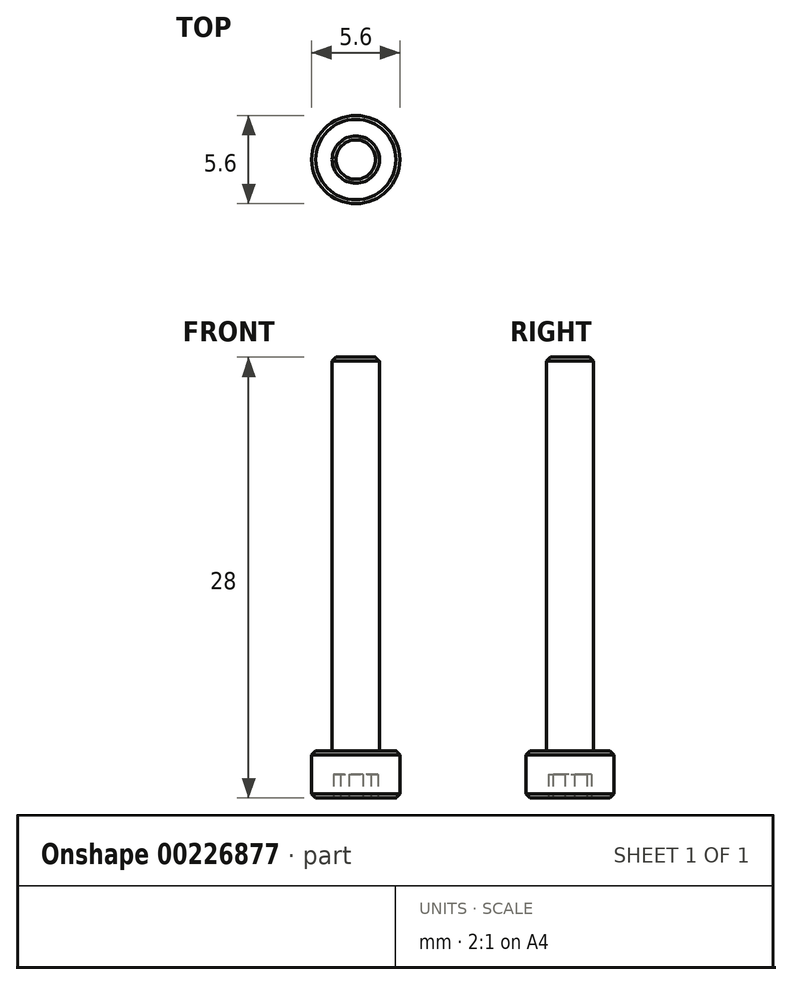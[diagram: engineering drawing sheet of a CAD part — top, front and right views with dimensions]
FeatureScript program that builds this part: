
annotation { "Feature Type Name" : "Feature", "Feature Type Description" : "" }
export const myFeature = defineFeature(function(context is Context, id is Id, definition is map)
    precondition{}
    {
        {
            var Q0;
            Q0=qCreatedBy(makeId("Top.planeOp"),FACE);
            var sketch = newSketch(context, id + "F0", { "sketchPlane" : qUnion([Q0])});
            skCircle(sketch, "E0", {"center": v(0, 0) * mm, "radius": 1.5 * mm});
            skSolve(sketch);
        }
        {
            var Q0;
            Q0=qSketchRegion(id+"F0",true);
            extrude(context, id + "F1", {"entities" : qUnion([Q0]), "depth" : 25 * mm});
        }
        {
            var Q0;
            Q0=qCreatedBy(makeId("Top.planeOp"),FACE);
            var sketch = newSketch(context, id + "F2", { "sketchPlane" : qUnion([Q0])});
            skCircle(sketch, "E1", {"center": v(0, 0) * mm, "radius": 2.8 * mm});
            skSolve(sketch);
        }
        {
            var Q0;
            Q0=qSketchRegion(id+"F2",true);
            extrude(context, id + "F3", {"entities" : qUnion([Q0]), "operationType" : NewBodyOperationType.ADD, "oppositeDirection" : true, "depth" : 3 * mm});
        }
        {
            var Q0;
            Q0=makeQuery(id+"F3.opExtrude","CAP_FACE",FACE,{"disambiguationData":[OSD([sQuery(id+"F2.wireOp",EDGE,"E1")])],"isStart":false});
            var sketch = newSketch(context, id + "F4", { "sketchPlane" : qUnion([Q0])});
            skCircle(sketch, "E2.cCircle", {"center": v(0, 0) * mm, "radius": 1.25 * mm, "construction": true});
            skLineSegment(sketch, "E2.0", {"start": v(1.41, -0.3) * mm, "end": v(0.45, -1.37) * mm});
            skLineSegment(sketch, "E2.1", {"start": v(0.45, -1.37) * mm, "end": v(-0.97, -1.07) * mm});
            skLineSegment(sketch, "E2.2", {"start": v(-0.97, -1.07) * mm, "end": v(-1.41, 0.3) * mm});
            skLineSegment(sketch, "E2.3", {"start": v(-1.41, 0.3) * mm, "end": v(-0.45, 1.37) * mm});
            skLineSegment(sketch, "E2.4", {"start": v(-0.45, 1.37) * mm, "end": v(0.97, 1.07) * mm});
            skLineSegment(sketch, "E2.5", {"start": v(0.97, 1.07) * mm, "end": v(1.41, -0.3) * mm});
            skPoint(sketch, "E2.0.midPoint", {"position": v(0.93, -0.84) * mm});
            skSolve(sketch);
        }
        {
            var Q0;
            Q0=makeQuery(id+"F4.imprint","IMPRINT",FACE,{"disambiguationData":[TD([[makeQuery(id+"F4.imprint","IMPRINT",EDGE,{"derivedFrom":sQuery(id+"F4.wireOp",EDGE,"E2.0")}),-1.0]])]});
            extrude(context, id + "F5", {"entities" : qUnion([Q0]), "operationType" : NewBodyOperationType.REMOVE, "oppositeDirection" : true, "depth" : 1.5 * mm});
        }
        {
            var Q0;
            Q0=makeQuery(id+"F3.opExtrude","CAP_EDGE",EDGE,{"disambiguationData":[OSD([sQuery(id+"F2.wireOp",EDGE,"E1")])],"isStart":false});
            var Q1;
            Q1=makeQuery(id+"F1.opExtrude","CAP_EDGE",EDGE,{"disambiguationData":[OSD([sQuery(id+"F0.wireOp",EDGE,"E0")])],"isStart":false});
            var Q2;
            Q2=makeQuery(id+"F3.opExtrude","CAP_EDGE",EDGE,{"disambiguationData":[OSD([sQuery(id+"F2.wireOp",EDGE,"E1")])],"isStart":true});
            chamfer(context, id + "F6", {"entities" : qUnion([Q0, Q1, Q2]), "width" : .25 * mm, "tangentPropagation" : true});
        }
    });
